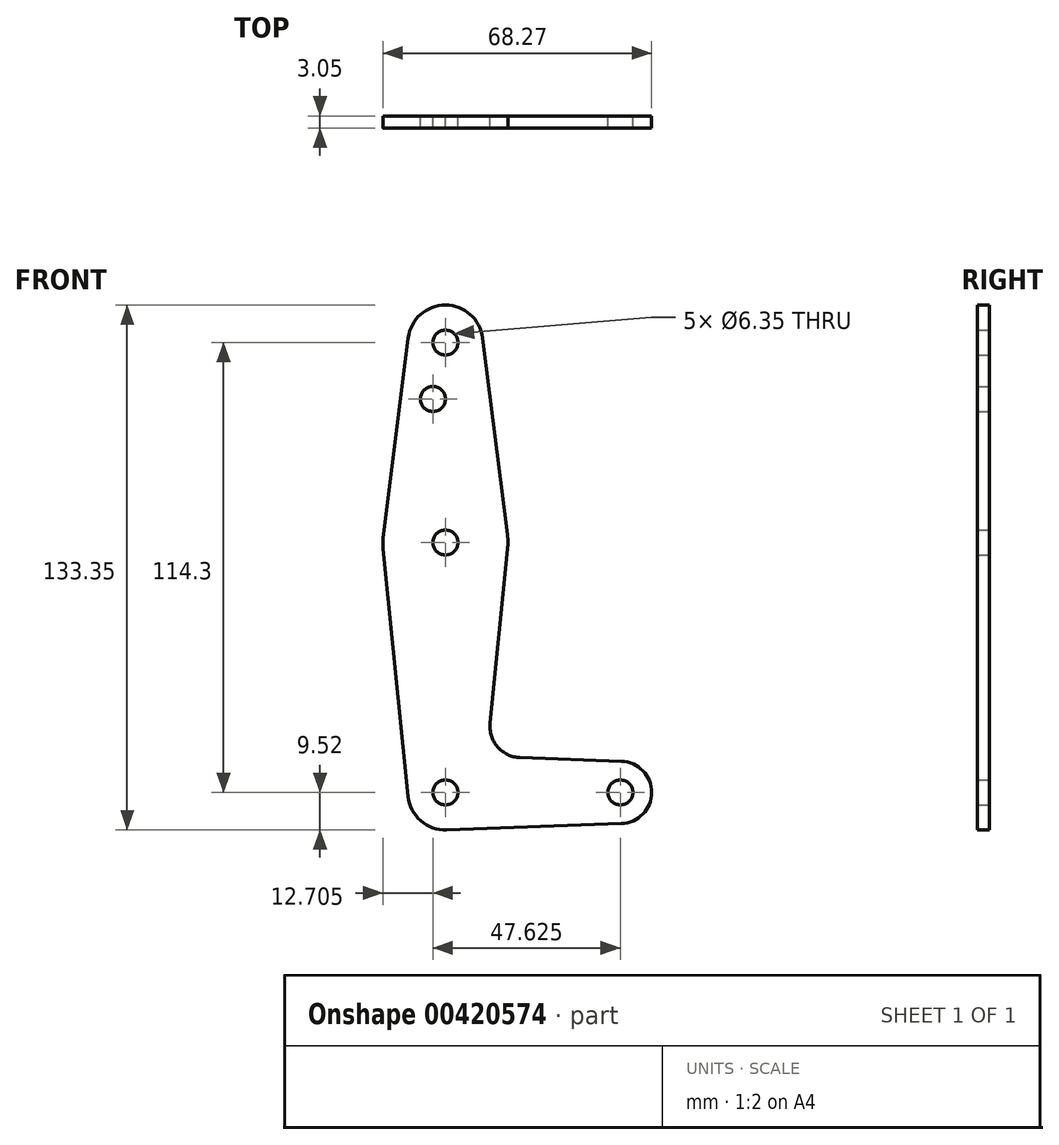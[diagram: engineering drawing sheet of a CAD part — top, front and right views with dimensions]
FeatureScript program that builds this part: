
annotation { "Feature Type Name" : "Feature", "Feature Type Description" : "" }
export const myFeature = defineFeature(function(context is Context, id is Id, definition is map)
    precondition{}
    {
        {
            var Q0;
            Q0=qCreatedBy(makeId("Front.planeOp"),FACE);
            var sketch = newSketch(context, id + "F0", { "sketchPlane" : qUnion([Q0])});
            skLineSegment(sketch, "E0", {"start": v(0, 0) * mm, "end": v(0, 63.5) * mm, "construction": true});
            skLineSegment(sketch, "E1", {"start": v(0, 63.5) * mm, "end": v(0, 0) * mm, "construction": true});
            skLineSegment(sketch, "E2", {"start": v(0, 0) * mm, "end": v(44.45, 0) * mm, "construction": true});
            skLineSegment(sketch, "E3", {"start": v(0, 63.5) * mm, "end": v(0, 114.3) * mm, "construction": true});
            skCircle(sketch, "E4", {"center": v(0, 0) * mm, "radius": 9.53 * mm});
            skCircle(sketch, "E5", {"center": v(44.45, 0) * mm, "radius": 7.94 * mm});
            skCircle(sketch, "E6", {"center": v(0, 114.3) * mm, "radius": 9.53 * mm});
            skCircle(sketch, "E7", {"center": v(0, 63.5) * mm, "radius": 15.88 * mm});
            skLineSegment(sketch, "E8", {"start": v(-15.75, 65.48) * mm, "end": v(-9.45, 115.5) * mm});
            skLineSegment(sketch, "E9", {"start": v(15.75, 65.48) * mm, "end": v(9.45, 115.5) * mm});
            skLineSegment(sketch, "E10", {"start": v(-15.8, 61.91) * mm, "end": v(-9.48, -0.95) * mm});
            skLineSegment(sketch, "E11", {"start": v(15.8, 61.91) * mm, "end": v(11.34, 17.6) * mm});
            skLineSegment(sketch, "E12", {"start": v(0.34, -9.52) * mm, "end": v(44.73, -7.93) * mm});
            skLineSegment(sketch, "E13", {"start": v(18.97, 8.85) * mm, "end": v(44.73, 7.93) * mm});
            skCircle(sketch, "E14", {"center": v(0, 114.3) * mm, "radius": 3.18 * mm});
            skCircle(sketch, "E15", {"center": v(0, 63.5) * mm, "radius": 3.18 * mm});
            skCircle(sketch, "E16", {"center": v(0, 0) * mm, "radius": 3.18 * mm});
            skCircle(sketch, "E17", {"center": v(-3.18, 99.96) * mm, "radius": 3.18 * mm});
            skCircle(sketch, "E18", {"center": v(44.45, 0) * mm, "radius": 3.18 * mm});
            skArc(sketch, "E19.filletArc", {"start": v(11.34, 17.6) * mm, "mid": v(13.26, 11.57) * mm, "end": v(18.97, 8.85) * mm});
            skPoint(sketch, "E20", {"position": v(-3.17, 63.43) * mm});
            skSolve(sketch);
        }
        {
            var Q0;
            Q0 = qSketchRegion(id + "F0", true);
            extrude(context, id + "F1", {"entities" : qUnion([Q0]), "depth" : 3.05 * mm});
        }
    });
